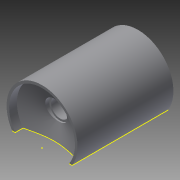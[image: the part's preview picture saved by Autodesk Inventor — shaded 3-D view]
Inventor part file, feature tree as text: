
AUTODESK INVENTOR PART (.ipt)
format: ipt  version: 2014 (Build 180170000, 170)  size: 598,016 bytes
history: native  units: mm
features: sketch x9, extrude x5, chamfer x3, plane x2, fillet x2, loft x1, projected_geometry x1
ambient origin geometry x8: Origin, YZ Plane, XZ Plane, XY Plane, X Axis, Y Axis, Z Axis, Center Point
bodies: Solid1 (feature_tree)
feature tree (23):
  extrude  "Extrusion1"  Depth=45.0mm
  sketch  "Sketch2"  dims[d2=55.0mm d3=5.0mm]
  plane  "Work Plane1"
  extrude  "Extrusion2"  Depth=5.0mm
  chamfer  "Chamfer1"  Distance=160.0mm
  sketch  "Sketch4"  dims[d7=70.0mm d8=-30.0mm]
  sketch  "Sketch5"  dims[d9=19.0mm d10=0.0mm d11=55.0mm d12=17.0mm d13=45.0deg]
  plane  "Work Plane2"
  extrude  "Extrusion3"  [1 undecoded]
  loft  "Loft1"
  extrude  "Extrusion4"  [1 undecoded]
  chamfer  "Chamfer2"  Distance=27.0mm
  extrude  "Extrusion5"  TaperAngle=0.0deg  [1 undecoded]
  chamfer  "Chamfer3"  Angle=90.0deg  [1 undecoded]
  fillet  "Fillet1"  Radius=10.0mm
  fillet  "Fillet2"  Radius=5.0mm
  sketch  "Sketch1"  dims[d0=90.0mm d1=45.0mm]
  sketch  "Sketch3"  dims[d4=5.0mm d5=160.0mm d6=0.0mm]
  projected_geometry  "Projected Loop1"
  sketch  "Sketch6"  dims[d14=33.0mm d15=-19.0mm]
  sketch  "Sketch7"  dims[d16=36.0mm d17=27.0mm d18=0.0mm]
  sketch  "Sketch8"  dims[d19=30.0mm d20=0.0mm d21=90.0deg d22=0.0mm d23=90.0deg d24=10.0mm d25=0.0mm]
  sketch  "Sketch9"  dims[d26=5.0mm d27=10.0mm d28=45.0deg d29=5.0mm d30=5.0mm d31=10.0mm d32=0.0mm d33=9.0mm d34=10.0mm d35=45.0deg d36=2.0mm d37=1.7mm]
note: 4 required parameter values undecoded (feature->parameter linkage not recoverable at this tier; creation-order binding heuristic only, values carry confidence <= 0.55)
